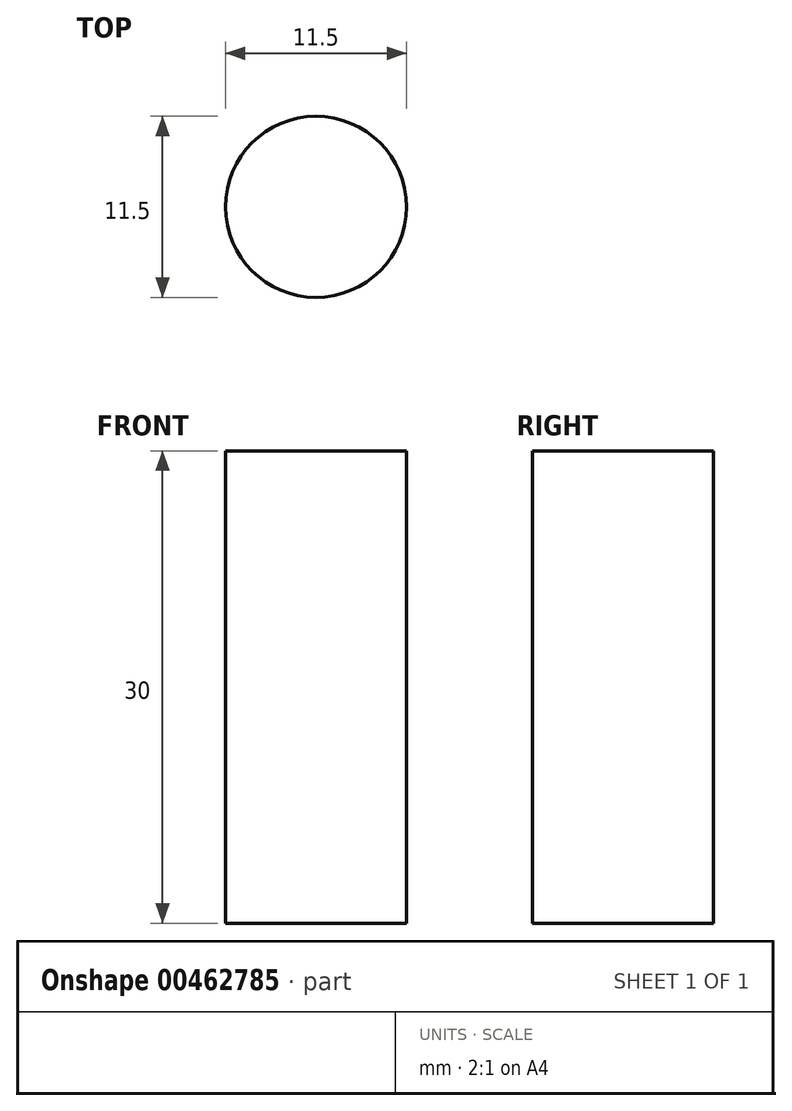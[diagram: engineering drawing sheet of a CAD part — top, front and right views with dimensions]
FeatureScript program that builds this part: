
annotation { "Feature Type Name" : "Feature", "Feature Type Description" : "" }
export const myFeature = defineFeature(function(context is Context, id is Id, definition is map)
    precondition{}
    {
        {
            var Q0;
            Q0=qCreatedBy(makeId("Top.planeOp"),FACE);
            var sketch = newSketch(context, id + "F0", { "sketchPlane" : qUnion([Q0])});
            skCircle(sketch, "E0", {"center": v(0, 0) * mm, "radius": 5.75 * mm});
            skSolve(sketch);
        }
        {
            var Q0;
            Q0=makeQuery(id+"F0.imprint","IMPRINT",FACE,{"disambiguationData":[TD([[makeQuery(id+"F0.imprint","IMPRINT",EDGE,{"derivedFrom":sQuery(id+"F0.wireOp",EDGE,"E0")}),1.0]])]});
            extrude(context, id + "F1", {"entities" : qUnion([Q0]), "depth" : 30 * mm});
        }
    });
